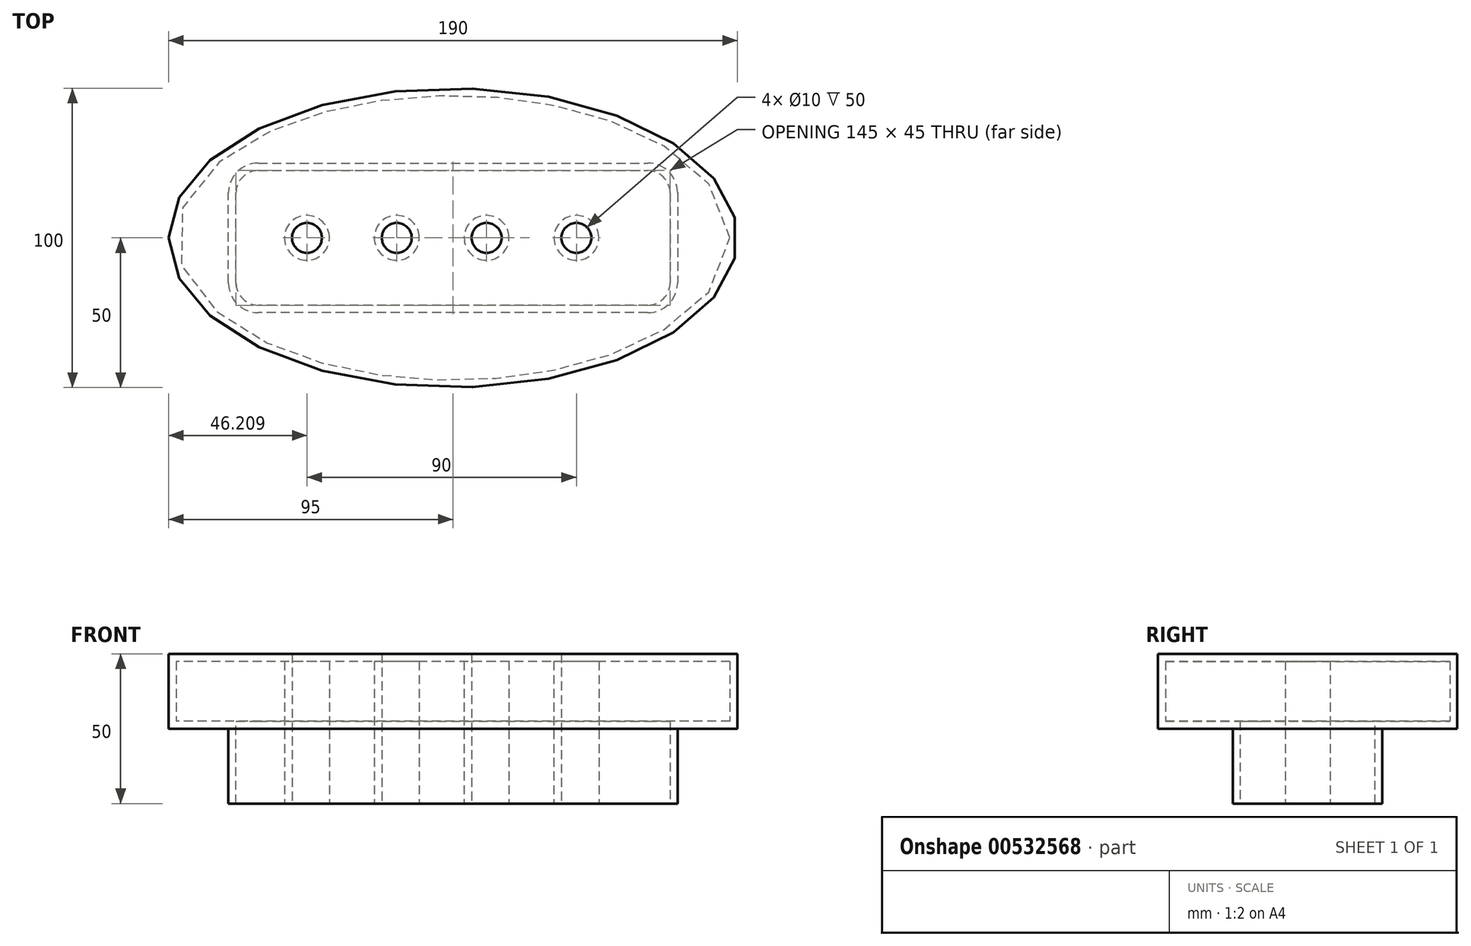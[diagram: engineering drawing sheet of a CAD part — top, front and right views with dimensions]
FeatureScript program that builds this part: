
annotation { "Feature Type Name" : "Feature", "Feature Type Description" : "" }
export const myFeature = defineFeature(function(context is Context, id is Id, definition is map)
    precondition{}
    {
        {
            var Q0;
            Q0=qCreatedBy(makeId("Top.planeOp"),FACE);
            var sketch = newSketch(context, id + "F0", { "sketchPlane" : qUnion([Q0])});
            skLineSegment(sketch, "E0.bottom", {"start": v(75, 25) * mm, "end": v(-75, 25) * mm});
            skLineSegment(sketch, "E0.top", {"start": v(75, -25) * mm, "end": v(-75, -25) * mm});
            skLineSegment(sketch, "E0.left", {"start": v(75, 25) * mm, "end": v(75, -25) * mm});
            skLineSegment(sketch, "E0.right", {"start": v(-75, 25) * mm, "end": v(-75, -25) * mm});
            skPoint(sketch, "E0.middle", {"position": v(0, 0) * mm});
            skPoint(sketch, "E1", {"position": v(0, 75) * mm});
            skPoint(sketch, "E2", {"position": v(100, 0) * mm});
            skSolve(sketch);
        }
        {
            var Q0;
            Q0=makeQuery(id+"F0.imprint","IMPRINT",FACE,{"disambiguationData":[TD([[makeQuery(id+"F0.imprint","IMPRINT",EDGE,{"derivedFrom":sQuery(id+"F0.wireOp",EDGE,"E0.bottom")}),1.0]])]});
            var Q1;
            Q1=sQuery(id+"F0.wireOp",EDGE,"Se1Qruzl-nVS9-5STv-RUCT-c2ObxEfhd4HU");
            extrude(context, id + "F1", {"entities" : qUnion([Q0]), "surfaceEntities" : qUnion([Q1]), "depth" : 25 * mm, "offsetDistance" : 25 * mm, "hasDraft" : true, "draftAngle" : 0 * degree});
        }
        {
            var Q0;
            Q0=makeQuery(id+"F1.opExtrude","SWEPT_EDGE",EDGE,{"disambiguationData":[OSD([sQuery(id+"F0.wireOp",EDGE,"E0.bottom"),sQuery(id+"F0.wireOp",EDGE,"E0.right")])]});
            var Q1;
            Q1=makeQuery(id+"F1.opExtrude","SWEPT_EDGE",EDGE,{"disambiguationData":[OSD([sQuery(id+"F0.wireOp",EDGE,"E0.top"),sQuery(id+"F0.wireOp",EDGE,"E0.right")])]});
            var Q2;
            Q2=makeQuery(id+"F1.opExtrude","SWEPT_EDGE",EDGE,{"disambiguationData":[OSD([sQuery(id+"F0.wireOp",EDGE,"E0.bottom"),sQuery(id+"F0.wireOp",EDGE,"E0.left")])]});
            var Q3;
            Q3=makeQuery(id+"F1.opExtrude","SWEPT_EDGE",EDGE,{"disambiguationData":[OSD([sQuery(id+"F0.wireOp",EDGE,"E0.top"),sQuery(id+"F0.wireOp",EDGE,"E0.left")])]});
            fillet(context, id + "F2", {"entities" : qUnion([Q0, Q1, Q2, Q3]), "radius" : 10 * mm, "tangentPropagation" : true, "allowEdgeOverflow" : false});
        }
        {
            var Q0;
            Q0=makeQuery(id+"F1.opExtrude","CAP_FACE",FACE,{"disambiguationData":[OSD([sQuery(id+"F0.wireOp",EDGE,"E0.bottom"),sQuery(id+"F0.wireOp",EDGE,"E0.top"),sQuery(id+"F0.wireOp",EDGE,"E0.left"),sQuery(id+"F0.wireOp",EDGE,"E0.right")])],"isStart":false});
            var sketch = newSketch(context, id + "F3", { "sketchPlane" : qUnion([Q0])});
            skEllipse(sketch, "E3", {"center": v(0, 0) * mm, "majorRadius": 50 * mm, "minorRadius": 95 * mm, "majorAxis": v(0, 1)});
            skPoint(sketch, "E4", {"position": v(0, 50) * mm});
            skPoint(sketch, "E5", {"position": v(95, 0) * mm});
            skSolve(sketch);
        }
        {
            var Q0;
            {var subQ3=sQuery(id+"F0.wireOp",EDGE,"E0.bottom");Q0=makeQuery(id+"F3.imprint","IMPRINT",FACE,{"disambiguationData":[TD([[makeQuery(id+"F3.imprint","IMPRINT",EDGE,{"derivedFrom":makeQuery(id+"F1.opExtrude","CAP_EDGE",EDGE,{"disambiguationData":[OSD([subQ3])],"isStart":false})}),1.0]])]});}
            var Q1;
            Q1=makeQuery(id+"F3.imprint","IMPRINT",FACE,{"disambiguationData":[TD([[makeQuery(id+"F3.imprint","IMPRINT",EDGE,{"derivedFrom":sQuery(id+"F3.wireOp",EDGE,"E3")}),1.0]])]});
            extrude(context, id + "F4", {"entities" : qUnion([Q0, Q1]), "operationType" : NewBodyOperationType.ADD, "depth" : 25 * mm, "offsetDistance" : 25 * mm});
        }
        {
            var Q0;
            Q0=makeQuery(id+"F0.imprint","IMPRINT",FACE,{"disambiguationData":[TD([[makeQuery(id+"F0.imprint","IMPRINT",EDGE,{"derivedFrom":sQuery(id+"F0.wireOp",EDGE,"E0.bottom")}),1.0]])]});
            var sketch = newSketch(context, id + "F5", { "sketchPlane" : qUnion([Q0])});
            skPoint(sketch, "E6", {"position": v(-48.8, 0) * mm});
            skPoint(sketch, "E7.1.0.0", {"position": v(-18.8, 0) * mm});
            skPoint(sketch, "E7.2.0.0", {"position": v(11.2, 0) * mm});
            skPoint(sketch, "E7.3.0.0", {"position": v(41.2, 0) * mm});
            skLineSegment(sketch, "E7.direction1", {"start": v(-48.8, 0) * mm, "end": v(-18.8, 0) * mm, "construction": true});
            skSolve(sketch);
        }
        {
            var Q0;
            Q0=sQuery(id+"F5.wireOp",VERTEX,"E6");
            var Q1;
            Q1=sQuery(id+"F5.wireOp",VERTEX,"E7.1.0.0");
            var Q2;
            Q2=sQuery(id+"F5.wireOp",VERTEX,"E7.2.0.0");
            var Q3;
            Q3=sQuery(id+"F5.wireOp",VERTEX,"E7.3.0.0");
            var Q4;
            Q4=makeQuery(id+"F1.opExtrude","SWEPT_BODY",BODY,{"disambiguationData":[OSD([sQuery(id+"F0.wireOp",EDGE,"E0.bottom"),sQuery(id+"F0.wireOp",EDGE,"E0.top"),sQuery(id+"F0.wireOp",EDGE,"E0.left"),sQuery(id+"F0.wireOp",EDGE,"E0.right")])]});
            hole(context, id + "F6", {"style" : HoleStyle.SIMPLE, "endStyle" : HoleEndStyle.THROUGH, "oppositeDirection" : true, "holeDiameter" : 10 * mm, "isTappedThrough" : true, "tappedDepth" : 12 * mm, "tapClearance" : 3, "locations" : qUnion([Q0, Q1, Q2, Q3]), "scope" : qUnion([Q4])});
        }
        {
            var Q0;
            Q0=makeQuery(id+"F1.opExtrude","CAP_FACE",FACE,{"disambiguationData":[OSD([sQuery(id+"F0.wireOp",EDGE,"E0.bottom"),sQuery(id+"F0.wireOp",EDGE,"E0.top"),sQuery(id+"F0.wireOp",EDGE,"E0.left"),sQuery(id+"F0.wireOp",EDGE,"E0.right")])],"isStart":true});
            shell(context, id + "F7", {"entities" : qUnion([Q0]), "thickness" : 2.5 * mm});
        }
    });
